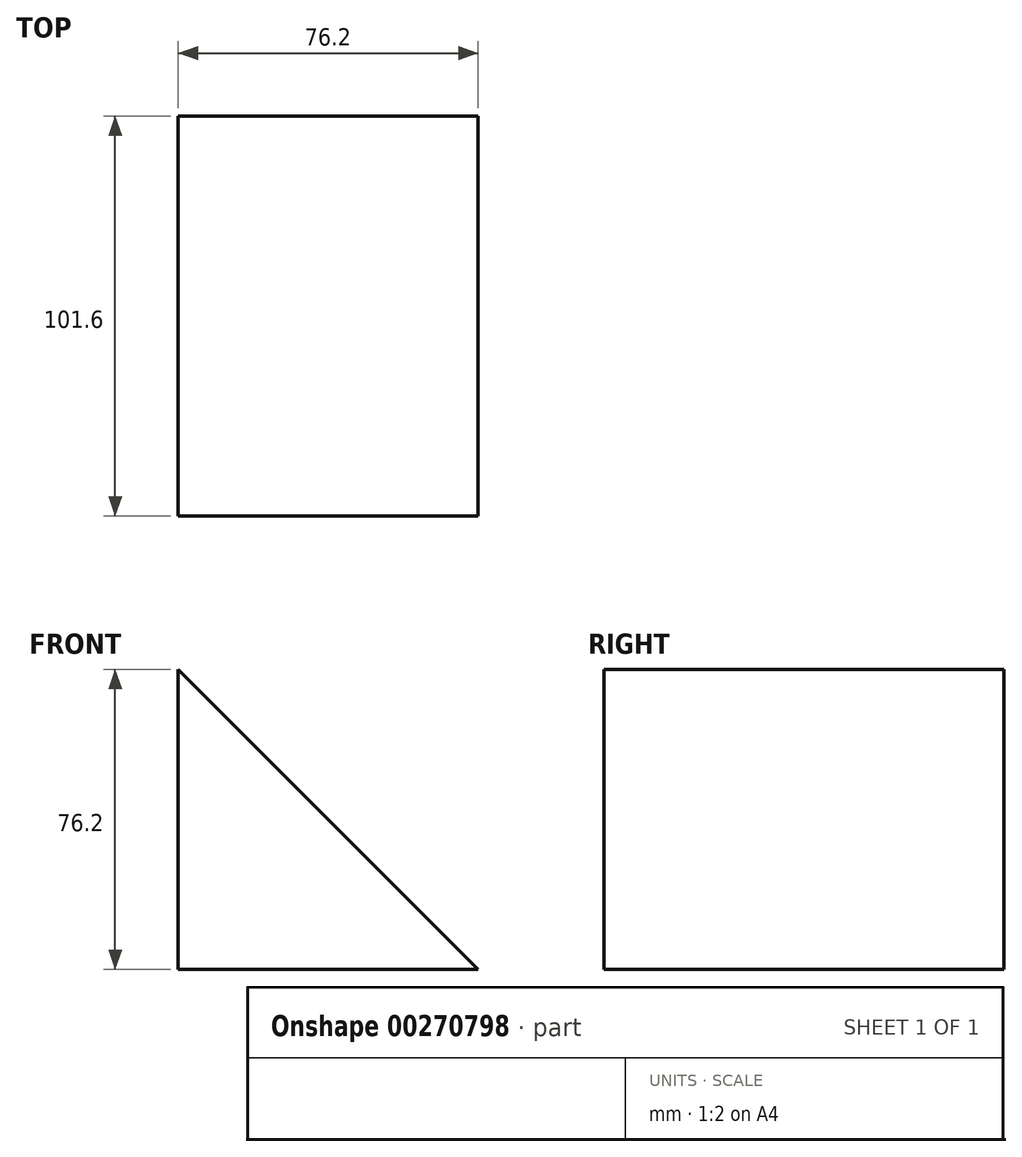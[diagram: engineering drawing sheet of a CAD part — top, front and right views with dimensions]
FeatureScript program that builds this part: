
annotation { "Feature Type Name" : "Feature", "Feature Type Description" : "" }
export const myFeature = defineFeature(function(context is Context, id is Id, definition is map)
    precondition{}
    {
        {
            var Q0;
            Q0=qCreatedBy(makeId("Front.planeOp"),FACE);
            var sketch = newSketch(context, id + "F0", { "sketchPlane" : qUnion([Q0])});
            skLineSegment(sketch, "E0", {"start": v(-47.74, 36.25) * mm, "end": v(-47.74, -39.95) * mm});
            skLineSegment(sketch, "E1", {"start": v(-47.74, -39.95) * mm, "end": v(28.46, -39.95) * mm});
            skLineSegment(sketch, "E2", {"start": v(-47.74, 36.25) * mm, "end": v(28.46, -39.95) * mm});
            skSolve(sketch);
        }
        {
            var Q0;
            Q0 = qSketchRegion(id + "F0", true);
            extrude(context, id + "F1", {"entities" : qUnion([Q0]), "depth" : 101.6 * mm});
        }
    });
